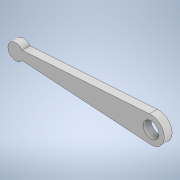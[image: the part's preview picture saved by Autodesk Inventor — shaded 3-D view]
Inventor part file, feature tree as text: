
AUTODESK INVENTOR PART (.ipt)
format: ipt  version: 2020.3 (Build 243373000, 373)  size: 108,544 bytes
history: native  units: mm
features: extrude x1, direct_edit x1, sketch x1, move_body x1
ambient origin geometry x8: Origin, YZ Plane, XZ Plane, XY Plane, X Axis, Y Axis, Z Axis, Center Point
bodies: Solid1 (feature_tree)
feature tree (4):
  extrude  "Extrusion1"  Depth=10.0mm
  direct_edit  "Direct Edit1"
  sketch  "Sketch1"  dims[d0=6.0mm d1=10.0mm d2=6.0mm d3=3.0mm d4=0.0mm d5=-21.75mm d6=0.0mm d7=0.0mm]
  move_body  "Move1"
